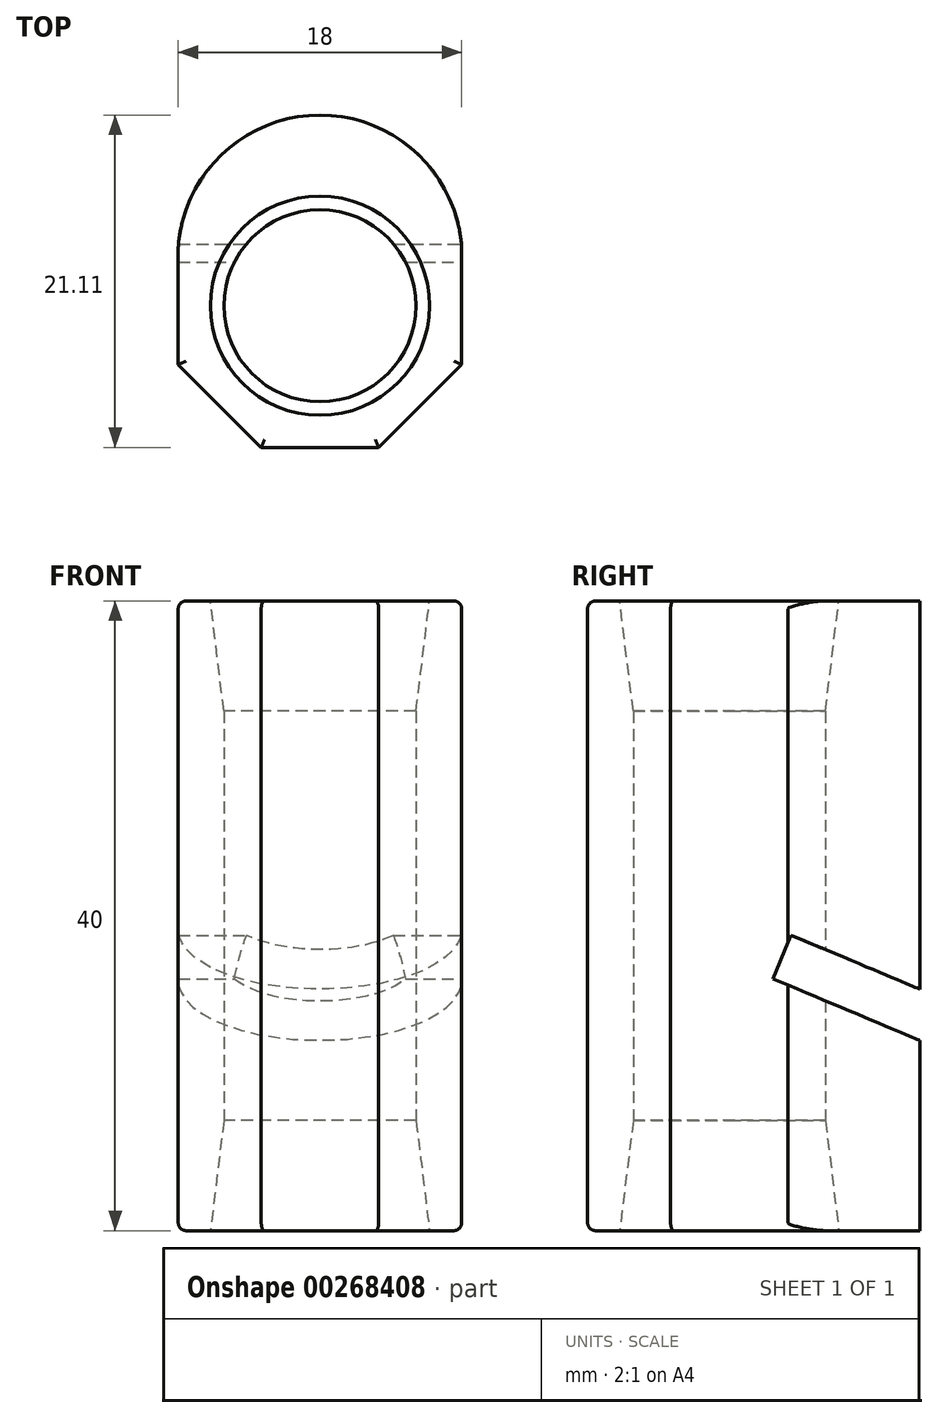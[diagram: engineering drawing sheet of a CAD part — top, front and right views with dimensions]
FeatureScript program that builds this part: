
annotation { "Feature Type Name" : "Feature", "Feature Type Description" : "" }
export const myFeature = defineFeature(function(context is Context, id is Id, definition is map)
    precondition{}
    {
        {
            var Q0;
            Q0=qCreatedBy(makeId("Top.planeOp"),FACE);
            var sketch = newSketch(context, id + "F0", { "sketchPlane" : qUnion([Q0])});
            skCircle(sketch, "E0", {"center": v(0, 0) * mm, "radius": 6.1 * mm});
            skPoint(sketch, "E1.0.midPoint", {"position": v(0, 9) * mm});
            skCircle(sketch, "E2", {"center": v(0, 0) * mm, "radius": 9 * mm, "construction": true});
            skLineSegment(sketch, "E3.2", {"start": v(9, 3.73) * mm, "end": v(9, -3.73) * mm});
            skLineSegment(sketch, "E3.3", {"start": v(9, -3.73) * mm, "end": v(3.73, -9) * mm});
            skLineSegment(sketch, "E3.4", {"start": v(3.73, -9) * mm, "end": v(-3.73, -9) * mm});
            skLineSegment(sketch, "E3.5", {"start": v(-3.73, -9) * mm, "end": v(-9, -3.73) * mm});
            skLineSegment(sketch, "E3.6", {"start": v(-9, -3.73) * mm, "end": v(-9, 3.73) * mm});
            skArc(sketch, "E4", {"start": v(9, 3.73) * mm, "mid": v(0, 12.11) * mm, "end": v(-9, 3.73) * mm});
            skSolve(sketch);
        }
        {
            var Q0;
            Q0=makeQuery(id+"F0.imprint","IMPRINT",FACE,{"disambiguationData":[TD([[makeQuery(id+"F0.imprint","IMPRINT",EDGE,{"derivedFrom":sQuery(id+"F0.wireOp",EDGE,"E0")}),-1.0]])]});
            extrude(context, id + "F1", {"entities" : qUnion([Q0]), "depth" : 40 * mm, "offsetDistance" : 25 * mm});
        }
        {
            var Q0;
            Q0=qCreatedBy(makeId("Right.planeOp"),FACE);
            var sketch = newSketch(context, id + "F2", { "sketchPlane" : qUnion([Q0])});
            skLineSegment(sketch, "E5.0.1.0", {"start": v(14.07, 14.51) * mm, "end": v(3.93, 18.77) * mm});
            skLineSegment(sketch, "E5.0.1.1", {"start": v(12.9, 11.74) * mm, "end": v(14.07, 14.51) * mm});
            skLineSegment(sketch, "E5.0.1.2", {"start": v(2.77, 16) * mm, "end": v(12.9, 11.74) * mm});
            skLineSegment(sketch, "E5.0.1.3", {"start": v(2.77, 16) * mm, "end": v(3.93, 18.77) * mm});
            skLineSegment(sketch, "E5.direction2", {"start": v(3.93, -1.23) * mm, "end": v(3.93, 18.77) * mm, "construction": true});
            skSolve(sketch);
        }
        {
            var Q0;
            Q0=makeQuery(id+"F2.imprint","IMPRINT",FACE,{"disambiguationData":[TD([[makeQuery(id+"F2.imprint","IMPRINT",EDGE,{"derivedFrom":sQuery(id+"F2.wireOp",EDGE,"E5.0.1.0")}),1.0]])]});
            var Q1;
            Q1=makeQuery(id+"F2.imprint","IMPRINT",FACE,{"disambiguationData":[TD([[makeQuery(id+"F2.imprint","IMPRINT",EDGE,{"derivedFrom":sQuery(id+"F2.wireOp",EDGE,"GdjSKvn1-YWNW-hjhV-CNt0-MgLaZjLN8e14")}),1.0]])]});
            extrude(context, id + "F3", {"entities" : qUnion([Q0, Q1]), "operationType" : NewBodyOperationType.REMOVE, "oppositeDirection" : true, "depth" : 25 * mm, "offsetDistance" : 25 * mm, "hasSecondDirection" : true, "secondDirectionOppositeDirection" : false, "secondDirectionDepth" : 25 * mm});
        }
        {
            var Q0;
            {var subQ0=sQuery(id+"F0.wireOp",EDGE,"1uds2ZHc-WtPi-VxFk-JlT4-WQfVxmiHtsB6");Q0=makeQuery(id+"F3.boolean.opBoolean","INTERSECT",EDGE,{"derivedFrom":[makeQuery(id+"F1.boolean.opBoolean","MERGE",FACE,{"derivedFrom":[makeQuery(id+"FCojyvOzqNuh9B3_0.opExtrude","SWEPT_FACE",FACE,{"disambiguationData":[OSD([subQ0])]}),makeQuery(id+"F1.opExtrude","SWEPT_FACE",FACE,{"disambiguationData":[OSD([subQ0])]})]}),makeQuery(id+"F3.opExtrude","SWEPT_FACE",FACE,{"disambiguationData":[OSD([sQuery(id+"F2.wireOp",EDGE,"E5.0.2.0")])]})]});}
            var Q1;
            {var subQ0=sQuery(id+"F0.wireOp",EDGE,"1uds2ZHc-WtPi-VxFk-JlT4-WQfVxmiHtsB6");Q1=makeQuery(id+"F3.boolean.opBoolean","INTERSECT",EDGE,{"derivedFrom":[makeQuery(id+"F1.boolean.opBoolean","MERGE",FACE,{"derivedFrom":[makeQuery(id+"FCojyvOzqNuh9B3_0.opExtrude","SWEPT_FACE",FACE,{"disambiguationData":[OSD([subQ0])]}),makeQuery(id+"F1.opExtrude","SWEPT_FACE",FACE,{"disambiguationData":[OSD([subQ0])]})]}),makeQuery(id+"F3.opExtrude","SWEPT_FACE",FACE,{"disambiguationData":[OSD([sQuery(id+"F2.wireOp",EDGE,"E5.0.2.2")])]})]});}
            var Q2;
            {var subQ0=sQuery(id+"F0.wireOp",EDGE,"1uds2ZHc-WtPi-VxFk-JlT4-WQfVxmiHtsB6");Q2=makeQuery(id+"F3.boolean.opBoolean","INTERSECT",EDGE,{"derivedFrom":[makeQuery(id+"F1.boolean.opBoolean","MERGE",FACE,{"derivedFrom":[makeQuery(id+"FCojyvOzqNuh9B3_0.opExtrude","SWEPT_FACE",FACE,{"disambiguationData":[OSD([subQ0])]}),makeQuery(id+"F1.opExtrude","SWEPT_FACE",FACE,{"disambiguationData":[OSD([subQ0])]})]}),makeQuery(id+"F3.opExtrude","SWEPT_FACE",FACE,{"disambiguationData":[OSD([sQuery(id+"F2.wireOp",EDGE,"E5.0.1.0")])]})]});}
            var Q3;
            {var subQ0=sQuery(id+"F0.wireOp",EDGE,"1uds2ZHc-WtPi-VxFk-JlT4-WQfVxmiHtsB6");Q3=makeQuery(id+"F3.boolean.opBoolean","INTERSECT",EDGE,{"derivedFrom":[makeQuery(id+"F1.boolean.opBoolean","MERGE",FACE,{"derivedFrom":[makeQuery(id+"FCojyvOzqNuh9B3_0.opExtrude","SWEPT_FACE",FACE,{"disambiguationData":[OSD([subQ0])]}),makeQuery(id+"F1.opExtrude","SWEPT_FACE",FACE,{"disambiguationData":[OSD([subQ0])]})]}),makeQuery(id+"F3.opExtrude","SWEPT_FACE",FACE,{"disambiguationData":[OSD([sQuery(id+"F2.wireOp",EDGE,"E5.0.1.2")])]})]});}
            var Q4;
            {var subQ0=sQuery(id+"F0.wireOp",EDGE,"1uds2ZHc-WtPi-VxFk-JlT4-WQfVxmiHtsB6");Q4=makeQuery(id+"F3.boolean.opBoolean","INTERSECT",EDGE,{"derivedFrom":[makeQuery(id+"F1.boolean.opBoolean","MERGE",FACE,{"derivedFrom":[makeQuery(id+"FCojyvOzqNuh9B3_0.opExtrude","SWEPT_FACE",FACE,{"disambiguationData":[OSD([subQ0])]}),makeQuery(id+"F1.opExtrude","SWEPT_FACE",FACE,{"disambiguationData":[OSD([subQ0])]})]}),makeQuery(id+"F3.opExtrude","SWEPT_FACE",FACE,{"disambiguationData":[OSD([sQuery(id+"F2.wireOp",EDGE,"J8dbItgX-bJHc-ha2m-F6V7-KSgbCjjJBfER")])]})]});}
            var Q5;
            {var subQ0=sQuery(id+"F0.wireOp",EDGE,"1uds2ZHc-WtPi-VxFk-JlT4-WQfVxmiHtsB6");Q5=makeQuery(id+"F3.boolean.opBoolean","INTERSECT",EDGE,{"derivedFrom":[makeQuery(id+"F1.boolean.opBoolean","MERGE",FACE,{"derivedFrom":[makeQuery(id+"FCojyvOzqNuh9B3_0.opExtrude","SWEPT_FACE",FACE,{"disambiguationData":[OSD([subQ0])]}),makeQuery(id+"F1.opExtrude","SWEPT_FACE",FACE,{"disambiguationData":[OSD([subQ0])]})]}),makeQuery(id+"F3.opExtrude","SWEPT_FACE",FACE,{"disambiguationData":[OSD([sQuery(id+"F2.wireOp",EDGE,"BaCOsYNs-gHyz-LfZ9-6YQV-WEOo2sPEaBoS")])]})]});}
            var Q6;
            {var subQ0=sQuery(id+"F0.wireOp",EDGE,"1uds2ZHc-WtPi-VxFk-JlT4-WQfVxmiHtsB6");Q6=makeQuery(id+"F3.boolean.opBoolean","INTERSECT",EDGE,{"disambiguationData":[OD(1.0)],"derivedFrom":[makeQuery(id+"F1.boolean.opBoolean","MERGE",FACE,{"derivedFrom":[makeQuery(id+"FCojyvOzqNuh9B3_0.opExtrude","SWEPT_FACE",FACE,{"disambiguationData":[OSD([subQ0])]}),makeQuery(id+"F1.opExtrude","SWEPT_FACE",FACE,{"disambiguationData":[OSD([subQ0])]})]}),makeQuery(id+"F3.opExtrude","SWEPT_FACE",FACE,{"disambiguationData":[OSD([sQuery(id+"F2.wireOp",EDGE,"vIR03PF7-ik9o-uVv7-byYm-V89zexL9JbVE")])]})]});}
            var Q7;
            {var subQ0=sQuery(id+"F0.wireOp",EDGE,"1uds2ZHc-WtPi-VxFk-JlT4-WQfVxmiHtsB6");Q7=makeQuery(id+"F3.boolean.opBoolean","INTERSECT",EDGE,{"disambiguationData":[OD(0.0)],"derivedFrom":[makeQuery(id+"F1.boolean.opBoolean","MERGE",FACE,{"derivedFrom":[makeQuery(id+"FCojyvOzqNuh9B3_0.opExtrude","SWEPT_FACE",FACE,{"disambiguationData":[OSD([subQ0])]}),makeQuery(id+"F1.opExtrude","SWEPT_FACE",FACE,{"disambiguationData":[OSD([subQ0])]})]}),makeQuery(id+"F3.opExtrude","SWEPT_FACE",FACE,{"disambiguationData":[OSD([sQuery(id+"F2.wireOp",EDGE,"vIR03PF7-ik9o-uVv7-byYm-V89zexL9JbVE")])]})]});}
            var Q8;
            Q8=makeQuery(id+"F1.opExtrude","CAP_EDGE",EDGE,{"disambiguationData":[OSD([sQuery(id+"F0.wireOp",EDGE,"E3.4")])],"isStart":true});
            var Q9;
            Q9=makeQuery(id+"F1.opExtrude","CAP_EDGE",EDGE,{"disambiguationData":[OSD([sQuery(id+"F0.wireOp",EDGE,"E3.3")])],"isStart":true});
            var Q10;
            Q10=makeQuery(id+"F1.opExtrude","CAP_EDGE",EDGE,{"disambiguationData":[OSD([sQuery(id+"F0.wireOp",EDGE,"E3.2")])],"isStart":true});
            var Q11;
            Q11=makeQuery(id+"F1.opExtrude","CAP_EDGE",EDGE,{"disambiguationData":[OSD([sQuery(id+"F0.wireOp",EDGE,"E3.1")])],"isStart":true});
            var Q12;
            Q12=makeQuery(id+"F1.opExtrude","CAP_EDGE",EDGE,{"disambiguationData":[OSD([sQuery(id+"F0.wireOp",EDGE,"E3.0")])],"isStart":true});
            var Q13;
            Q13=makeQuery(id+"F1.opExtrude","CAP_EDGE",EDGE,{"disambiguationData":[OSD([sQuery(id+"F0.wireOp",EDGE,"E3.7")])],"isStart":true});
            var Q14;
            Q14=makeQuery(id+"F1.opExtrude","CAP_EDGE",EDGE,{"disambiguationData":[OSD([sQuery(id+"F0.wireOp",EDGE,"E3.6")])],"isStart":true});
            var Q15;
            Q15=makeQuery(id+"F1.opExtrude","CAP_EDGE",EDGE,{"disambiguationData":[OSD([sQuery(id+"F0.wireOp",EDGE,"E3.5")])],"isStart":true});
            var Q16;
            Q16=makeQuery(id+"F1.opExtrude","CAP_EDGE",EDGE,{"disambiguationData":[OSD([sQuery(id+"F0.wireOp",EDGE,"E3.4")])],"isStart":false});
            var Q17;
            Q17=makeQuery(id+"F1.opExtrude","CAP_EDGE",EDGE,{"disambiguationData":[OSD([sQuery(id+"F0.wireOp",EDGE,"E3.3")])],"isStart":false});
            var Q18;
            Q18=makeQuery(id+"F1.opExtrude","CAP_EDGE",EDGE,{"disambiguationData":[OSD([sQuery(id+"F0.wireOp",EDGE,"E3.2")])],"isStart":false});
            var Q19;
            Q19=makeQuery(id+"F1.opExtrude","CAP_EDGE",EDGE,{"disambiguationData":[OSD([sQuery(id+"F0.wireOp",EDGE,"E3.5")])],"isStart":false});
            var Q20;
            Q20=makeQuery(id+"F1.opExtrude","CAP_EDGE",EDGE,{"disambiguationData":[OSD([sQuery(id+"F0.wireOp",EDGE,"E3.6")])],"isStart":false});
            var Q21;
            Q21=makeQuery(id+"F1.opExtrude","CAP_EDGE",EDGE,{"disambiguationData":[OSD([sQuery(id+"F0.wireOp",EDGE,"E3.7")])],"isStart":false});
            var Q22;
            Q22=makeQuery(id+"F1.opExtrude","CAP_EDGE",EDGE,{"disambiguationData":[OSD([sQuery(id+"F0.wireOp",EDGE,"E3.0")])],"isStart":false});
            var Q23;
            Q23=makeQuery(id+"F1.opExtrude","CAP_EDGE",EDGE,{"disambiguationData":[OSD([sQuery(id+"F0.wireOp",EDGE,"E3.1")])],"isStart":false});
            fillet(context, id + "F4", {"entities" : qUnion([Q0, Q1, Q2, Q3, Q4, Q5, Q6, Q7, Q8, Q9, Q10, Q11, Q12, Q13, Q14, Q15, Q16, Q17, Q18, Q19, Q20, Q21, Q22, Q23]), "radius" : 0.5 * mm, "tangentPropagation" : true, "allowEdgeOverflow" : false});
        }
        {
            var Q0;
            Q0=makeQuery(id+"F1.opExtrude","CAP_EDGE",EDGE,{"disambiguationData":[OSD([sQuery(id+"F0.wireOp",EDGE,"E0")])],"isStart":false});
            var Q1;
            Q1=makeQuery(id+"F1.opExtrude","CAP_EDGE",EDGE,{"disambiguationData":[OSD([sQuery(id+"F0.wireOp",EDGE,"E0")])],"isStart":true});
            chamfer(context, id + "F5", {"entities" : qUnion([Q0, Q1]), "chamferType" : ChamferType.OFFSET_ANGLE, "width" : 7 * mm, "oppositeDirection" : false, "angle" : 7 * degree, "tangentPropagation" : true});
        }
    });
